# Revit family: ITK by ZPAS_Гребенка кабельная вертикальная_47U
name_source: partatom
category: Обобщенные модели
units: mm (PartAtom-declared; Revit-internal decimal feet)

## family parameters
Всегда вертикально = Да
Может служить основой для арматурных стержней = Нет
На основе рабочей плоскости = Нет
Общий = Нет
При загрузке вырезать с полостями = Нет
Размер круглого соединителя = Использовать диаметр
Тип детали = Нормальный
Точка расчета площади = Нет

## types (2) — shared parameters
ADSK_URL страницы изделия = https://www.itk-group.ru
ADSK_Версия Revit = 2019
ADSK_Версия семейства = 1.0
ADSK_Группирование = I. ЩИТЫ И ПУЛЬТЫ
ADSK_Единица измерения = шт
ADSK_Завод-изготовитель = IEK
ADSK_Масса = 7
ADSK_Материал наименование = Листовая сталь
ADSK_Наименование = by ZPAS
IEK_URL = https://www.itk-group.ru
IEK_Описание = Крепится без инструментов к 19-дюймовым монтажным профилям.
IEK_Цена за единицу = 11181.4
KSI_CMa_Строительные материалы = 10.03.02.06
KSI_CPr_Строительные изделия = 61.1.04.08
URL = https://www.iek.ru
Высота = 2067 мм
Глубина = 12 мм
Изготовитель = ITK
Тип монтажа = Установка на захваты
Ширина = 140 мм

## per-type parameters (varying)
| type | ADSK_Код изделия | Материал |
| В2066,9_Черный | ZP-CM05-47U-V | Окраска - RAL 9005 |
| В2066,9_Серый | ZP-CM35-47U-V | Окраска - RAL 7035 |
